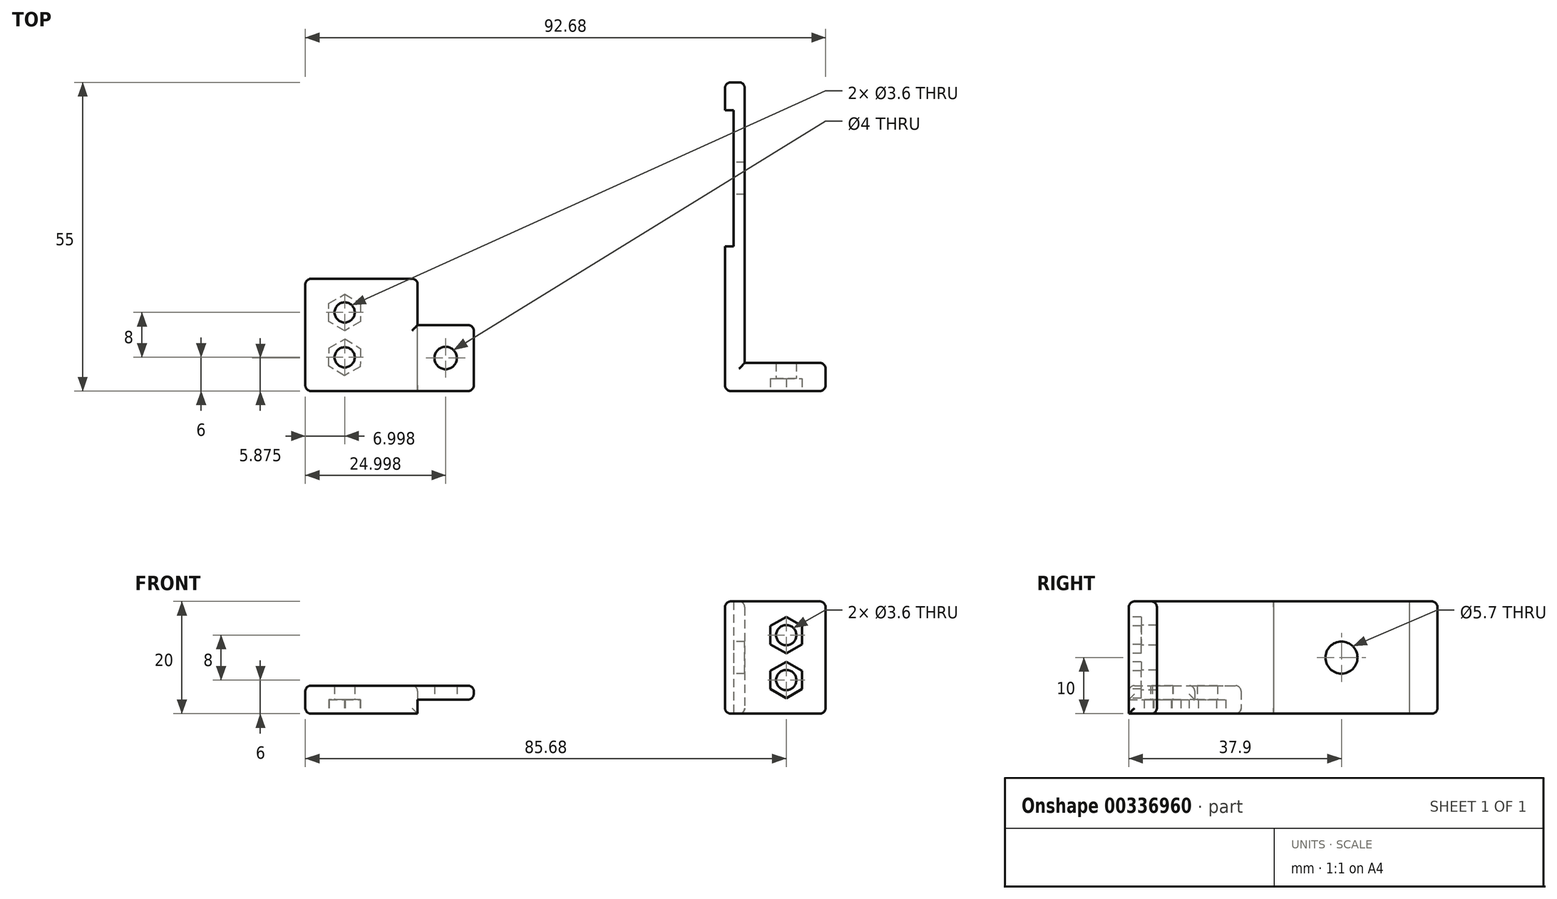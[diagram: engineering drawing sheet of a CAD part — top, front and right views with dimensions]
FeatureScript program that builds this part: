
annotation { "Feature Type Name" : "Feature", "Feature Type Description" : "" }
export const myFeature = defineFeature(function(context is Context, id is Id, definition is map)
    precondition{}
    {
        {
            var Q0;
            Q0=qCreatedBy(makeId("Top.planeOp"),FACE);
            var sketch = newSketch(context, id + "F0", { "sketchPlane" : qUnion([Q0])});
            skLineSegment(sketch, "E0", {"start": v(0, 0) * mm, "end": v(0, 25.8) * mm});
            skLineSegment(sketch, "E1", {"start": v(0, 25.8) * mm, "end": v(1.5, 25.8) * mm});
            skLineSegment(sketch, "E2", {"start": v(1.5, 25.8) * mm, "end": v(1.5, 50) * mm});
            skLineSegment(sketch, "E3", {"start": v(1.5, 50) * mm, "end": v(0, 50) * mm});
            skLineSegment(sketch, "E4", {"start": v(0, 50) * mm, "end": v(0, 55) * mm});
            skLineSegment(sketch, "E5", {"start": v(0, 55) * mm, "end": v(3.5, 55) * mm});
            skLineSegment(sketch, "E6", {"start": v(3.5, 55) * mm, "end": v(3.5, 5) * mm});
            skLineSegment(sketch, "E7", {"start": v(3.5, 5) * mm, "end": v(17.9, 5) * mm});
            skLineSegment(sketch, "E8", {"start": v(17.9, 5) * mm, "end": v(17.9, 0) * mm});
            skLineSegment(sketch, "E9", {"start": v(17.9, 0) * mm, "end": v(0, 0) * mm});
            skLineSegment(sketch, "E10.bottom", {"start": v(-74.78, 0) * mm, "end": v(-54.78, 0) * mm});
            skLineSegment(sketch, "E10.top", {"start": v(-74.78, 20) * mm, "end": v(-54.78, 20) * mm});
            skLineSegment(sketch, "E10.left", {"start": v(-74.78, 0) * mm, "end": v(-74.78, 20) * mm});
            skLineSegment(sketch, "E10.right", {"start": v(-54.78, 0) * mm, "end": v(-54.78, 20) * mm});
            skLineSegment(sketch, "E11.bottom", {"start": v(-54.78, 0) * mm, "end": v(-44.78, 0) * mm});
            skLineSegment(sketch, "E11.top", {"start": v(-54.78, 11.75) * mm, "end": v(-44.78, 11.75) * mm});
            skLineSegment(sketch, "E11.left", {"start": v(-54.78, 0) * mm, "end": v(-54.78, 11.75) * mm});
            skLineSegment(sketch, "E11.right", {"start": v(-44.78, 0) * mm, "end": v(-44.78, 11.75) * mm});
            skLineSegment(sketch, "E12", {"start": v(-67.78, 20) * mm, "end": v(-67.78, 0) * mm, "construction": true});
            skCircle(sketch, "E13", {"center": v(-67.78, 6) * mm, "radius": 1.8 * mm});
            skCircle(sketch, "E14", {"center": v(-67.78, 14) * mm, "radius": 1.8 * mm});
            skCircle(sketch, "E15.cCircle", {"center": v(-67.78, 14) * mm, "radius": 3.25 * mm, "construction": true});
            skLineSegment(sketch, "E15.0", {"start": v(-67.78, 10.75) * mm, "end": v(-70.6, 12.37) * mm});
            skLineSegment(sketch, "E15.1", {"start": v(-70.6, 12.38) * mm, "end": v(-70.6, 15.62) * mm});
            skLineSegment(sketch, "E15.2", {"start": v(-70.6, 15.63) * mm, "end": v(-67.78, 17.25) * mm});
            skLineSegment(sketch, "E15.3", {"start": v(-67.78, 17.25) * mm, "end": v(-64.97, 15.62) * mm});
            skLineSegment(sketch, "E15.4", {"start": v(-64.97, 15.62) * mm, "end": v(-64.97, 12.37) * mm});
            skLineSegment(sketch, "E15.5", {"start": v(-64.97, 12.37) * mm, "end": v(-67.78, 10.75) * mm});
            skCircle(sketch, "E16.cCircle", {"center": v(-67.78, 6) * mm, "radius": 3.25 * mm, "construction": true});
            skLineSegment(sketch, "E16.0", {"start": v(-70.56, 7.68) * mm, "end": v(-67.71, 9.25) * mm});
            skLineSegment(sketch, "E16.1", {"start": v(-67.71, 9.25) * mm, "end": v(-64.93, 7.56) * mm});
            skLineSegment(sketch, "E16.2", {"start": v(-64.93, 7.56) * mm, "end": v(-65, 4.32) * mm});
            skLineSegment(sketch, "E16.3", {"start": v(-65, 4.32) * mm, "end": v(-67.85, 2.75) * mm});
            skLineSegment(sketch, "E16.4", {"start": v(-67.85, 2.75) * mm, "end": v(-70.63, 4.44) * mm});
            skLineSegment(sketch, "E16.5", {"start": v(-70.63, 4.44) * mm, "end": v(-70.56, 7.68) * mm});
            skCircle(sketch, "E17", {"center": v(-49.78, 5.87) * mm, "radius": 2 * mm});
            skPoint(sketch, "E17.centerSnap0", {"position": v(-44.78, 5.87) * mm});
            skPoint(sketch, "E17.centerSnap1", {"position": v(-49.78, 11.75) * mm});
            skSolve(sketch);
        }
        {
            var Q0;
            Q0=makeQuery(id+"F0.imprint","IMPRINT",FACE,{"disambiguationData":[TD([[makeQuery(id+"F0.imprint","IMPRINT",EDGE,{"derivedFrom":sQuery(id+"F0.wireOp",EDGE,"E0")}),-1.0]])]});
            extrude(context, id + "F1", {"entities" : qUnion([Q0]), "depth" : 20 * mm});
        }
        {
            var Q0;
            Q0=makeQuery(id+"F1.opExtrude","SWEPT_FACE",FACE,{"disambiguationData":[OSD([sQuery(id+"F0.wireOp",EDGE,"E9")])]});
            var sketch = newSketch(context, id + "F2", { "sketchPlane" : qUnion([Q0])});
            skLineSegment(sketch, "E18", {"start": v(10.9, 0) * mm, "end": v(10.9, 20) * mm, "construction": true});
            skCircle(sketch, "E19", {"center": v(10.9, 6) * mm, "radius": 1.8 * mm});
            skCircle(sketch, "E20", {"center": v(10.9, 14) * mm, "radius": 1.8 * mm});
            skCircle(sketch, "E21.cCircle", {"center": v(10.9, 14) * mm, "radius": 3.25 * mm, "construction": true});
            skLineSegment(sketch, "E21.0", {"start": v(10.9, 10.75) * mm, "end": v(8.09, 12.37) * mm});
            skLineSegment(sketch, "E21.1", {"start": v(8.09, 12.38) * mm, "end": v(8.09, 15.62) * mm});
            skLineSegment(sketch, "E21.2", {"start": v(8.09, 15.62) * mm, "end": v(10.9, 17.25) * mm});
            skLineSegment(sketch, "E21.3", {"start": v(10.9, 17.25) * mm, "end": v(13.71, 15.62) * mm});
            skLineSegment(sketch, "E21.4", {"start": v(13.71, 15.62) * mm, "end": v(13.71, 12.37) * mm});
            skLineSegment(sketch, "E21.5", {"start": v(13.71, 12.38) * mm, "end": v(10.9, 10.75) * mm});
            skCircle(sketch, "E22.cCircle", {"center": v(10.9, 6) * mm, "radius": 3.25 * mm, "construction": true});
            skLineSegment(sketch, "E22.0", {"start": v(10.9, 9.25) * mm, "end": v(13.71, 7.63) * mm});
            skLineSegment(sketch, "E22.1", {"start": v(13.71, 7.63) * mm, "end": v(13.71, 4.38) * mm});
            skLineSegment(sketch, "E22.2", {"start": v(13.71, 4.38) * mm, "end": v(10.9, 2.75) * mm});
            skLineSegment(sketch, "E22.3", {"start": v(10.9, 2.75) * mm, "end": v(8.09, 4.37) * mm});
            skLineSegment(sketch, "E22.4", {"start": v(8.09, 4.37) * mm, "end": v(8.09, 7.62) * mm});
            skLineSegment(sketch, "E22.5", {"start": v(8.09, 7.62) * mm, "end": v(10.9, 9.25) * mm});
            skSolve(sketch);
        }
        {
            var Q0;
            Q0=makeQuery(id+"F2.imprint","IMPRINT",FACE,{"disambiguationData":[TD([[makeQuery(id+"F2.imprint","IMPRINT",EDGE,{"derivedFrom":sQuery(id+"F2.wireOp",EDGE,"E19")}),1.0]])]});
            var Q1;
            Q1=makeQuery(id+"F2.imprint","IMPRINT",FACE,{"disambiguationData":[TD([[makeQuery(id+"F2.imprint","IMPRINT",EDGE,{"derivedFrom":sQuery(id+"F2.wireOp",EDGE,"E20")}),1.0]])]});
            extrude(context, id + "F3", {"entities" : qUnion([Q0, Q1]), "operationType" : NewBodyOperationType.REMOVE, "oppositeDirection" : true, "depth" : 5 * mm});
        }
        {
            var Q0;
            Q0=makeQuery(id+"F2.imprint","IMPRINT",FACE,{"disambiguationData":[TD([[makeQuery(id+"F2.imprint","IMPRINT",EDGE,{"derivedFrom":sQuery(id+"F2.wireOp",EDGE,"E20")}),-1.0]])]});
            var Q1;
            Q1=makeQuery(id+"F2.imprint","IMPRINT",FACE,{"disambiguationData":[TD([[makeQuery(id+"F2.imprint","IMPRINT",EDGE,{"derivedFrom":sQuery(id+"F2.wireOp",EDGE,"E19")}),-1.0]])]});
            extrude(context, id + "F4", {"entities" : qUnion([Q0, Q1]), "operationType" : NewBodyOperationType.REMOVE, "oppositeDirection" : true, "depth" : 2.2 * mm});
        }
        {
            var Q0;
            Q0=makeQuery(id+"F1.opExtrude","SWEPT_FACE",FACE,{"disambiguationData":[OSD([sQuery(id+"F0.wireOp",EDGE,"E2")])]});
            var sketch = newSketch(context, id + "F5", { "sketchPlane" : qUnion([Q0])});
            skLineSegment(sketch, "E23", {"start": v(-50, 10) * mm, "end": v(-25.8, 10) * mm, "construction": true});
            skCircle(sketch, "E24", {"center": v(-37.9, 10) * mm, "radius": 2.85 * mm});
            skSolve(sketch);
        }
        {
            var Q0;
            Q0=makeQuery(id+"F5.imprint","IMPRINT",FACE,{"disambiguationData":[TD([[makeQuery(id+"F5.imprint","IMPRINT",EDGE,{"derivedFrom":sQuery(id+"F5.wireOp",EDGE,"E24")}),1.0]])]});
            extrude(context, id + "F6", {"entities" : qUnion([Q0]), "operationType" : NewBodyOperationType.REMOVE, "oppositeDirection" : true, "depth" : 25 * mm});
        }
        {
            var Q0;
            Q0=makeQuery(id+"F1.opExtrude","CAP_EDGE",EDGE,{"disambiguationData":[OSD([sQuery(id+"F0.wireOp",EDGE,"E7")])],"isStart":false});
            var Q1;
            Q1=makeQuery(id+"F1.opExtrude","CAP_EDGE",EDGE,{"disambiguationData":[OSD([sQuery(id+"F0.wireOp",EDGE,"E6")])],"isStart":false});
            var Q2;
            Q2=makeQuery(id+"F1.opExtrude","SWEPT_EDGE",EDGE,{"disambiguationData":[OSD([sQuery(id+"F0.wireOp",EDGE,"E5"),sQuery(id+"F0.wireOp",EDGE,"E6")])]});
            var Q3;
            Q3=makeQuery(id+"F1.opExtrude","CAP_EDGE",EDGE,{"disambiguationData":[OSD([sQuery(id+"F0.wireOp",EDGE,"E5")])],"isStart":false});
            var Q4;
            Q4=makeQuery(id+"F1.opExtrude","SWEPT_EDGE",EDGE,{"disambiguationData":[OSD([sQuery(id+"F0.wireOp",EDGE,"E4"),sQuery(id+"F0.wireOp",EDGE,"E5")])]});
            var Q5;
            Q5=makeQuery(id+"F1.opExtrude","CAP_EDGE",EDGE,{"disambiguationData":[OSD([sQuery(id+"F0.wireOp",EDGE,"E5")])],"isStart":true});
            var Q6;
            Q6=makeQuery(id+"F1.opExtrude","CAP_EDGE",EDGE,{"disambiguationData":[OSD([sQuery(id+"F0.wireOp",EDGE,"E6")])],"isStart":true});
            var Q7;
            Q7=makeQuery(id+"F1.opExtrude","CAP_EDGE",EDGE,{"disambiguationData":[OSD([sQuery(id+"F0.wireOp",EDGE,"E7")])],"isStart":true});
            var Q8;
            Q8=makeQuery(id+"F1.opExtrude","SWEPT_EDGE",EDGE,{"disambiguationData":[OSD([sQuery(id+"F0.wireOp",EDGE,"E7"),sQuery(id+"F0.wireOp",EDGE,"E8")])]});
            var Q9;
            Q9=makeQuery(id+"F1.opExtrude","CAP_EDGE",EDGE,{"disambiguationData":[OSD([sQuery(id+"F0.wireOp",EDGE,"E8")])],"isStart":true});
            var Q10;
            Q10=makeQuery(id+"F1.opExtrude","CAP_EDGE",EDGE,{"disambiguationData":[OSD([sQuery(id+"F0.wireOp",EDGE,"E8")])],"isStart":false});
            var Q11;
            Q11=makeQuery(id+"F1.opExtrude","SWEPT_EDGE",EDGE,{"disambiguationData":[OSD([sQuery(id+"F0.wireOp",EDGE,"E8"),sQuery(id+"F0.wireOp",EDGE,"E9")])]});
            var Q12;
            Q12=makeQuery(id+"F1.opExtrude","CAP_EDGE",EDGE,{"disambiguationData":[OSD([sQuery(id+"F0.wireOp",EDGE,"E0")])],"isStart":false});
            var Q13;
            Q13=makeQuery(id+"F1.opExtrude","CAP_EDGE",EDGE,{"disambiguationData":[OSD([sQuery(id+"F0.wireOp",EDGE,"E9")])],"isStart":false});
            var Q14;
            Q14=makeQuery(id+"F1.opExtrude","CAP_EDGE",EDGE,{"disambiguationData":[OSD([sQuery(id+"F0.wireOp",EDGE,"E4")])],"isStart":false});
            var Q15;
            Q15=makeQuery(id+"F1.opExtrude","CAP_EDGE",EDGE,{"disambiguationData":[OSD([sQuery(id+"F0.wireOp",EDGE,"E0")])],"isStart":true});
            var Q16;
            Q16=makeQuery(id+"F1.opExtrude","SWEPT_EDGE",EDGE,{"disambiguationData":[OSD([sQuery(id+"F0.wireOp",EDGE,"E0"),sQuery(id+"F0.wireOp",EDGE,"E9")])]});
            var Q17;
            Q17=makeQuery(id+"F1.opExtrude","CAP_EDGE",EDGE,{"disambiguationData":[OSD([sQuery(id+"F0.wireOp",EDGE,"E4")])],"isStart":true});
            fillet(context, id + "F7", {"entities" : qUnion([Q0, Q1, Q2, Q3, Q4, Q5, Q6, Q7, Q8, Q9, Q10, Q11, Q12, Q13, Q14, Q15, Q16, Q17]), "radius" : 1 * mm, "tangentPropagation" : true, "allowEdgeOverflow" : false});
        }
        {
            var Q0;
            Q0=makeQuery(id+"F0.imprint","IMPRINT",FACE,{"disambiguationData":[TD([[makeQuery(id+"F0.imprint","IMPRINT",EDGE,{"derivedFrom":sQuery(id+"F0.wireOp",EDGE,"E10.bottom")}),1.0]])]});
            extrude(context, id + "F8", {"entities" : qUnion([Q0]), "depth" : 5 * mm});
        }
        {
            var Q0;
            Q0=makeQuery(id+"F0.imprint","IMPRINT",FACE,{"disambiguationData":[TD([[makeQuery(id+"F0.imprint","IMPRINT",EDGE,{"derivedFrom":sQuery(id+"F0.wireOp",EDGE,"E13")}),-1.0]])]});
            var Q1;
            Q1=makeQuery(id+"F0.imprint","IMPRINT",FACE,{"disambiguationData":[TD([[makeQuery(id+"F0.imprint","IMPRINT",EDGE,{"derivedFrom":sQuery(id+"F0.wireOp",EDGE,"E14")}),-1.0]])]});
            extrude(context, id + "F9", {"entities" : qUnion([Q0, Q1]), "operationType" : NewBodyOperationType.ADD, "depth" : 5 * mm, "hasSecondDirection" : true, "secondDirectionOppositeDirection" : false, "secondDirectionDepth" : 2.5 * mm});
        }
        {
            var Q0;
            Q0=makeQuery(id+"F0.imprint","IMPRINT",FACE,{"disambiguationData":[TD([[makeQuery(id+"F0.imprint","IMPRINT",EDGE,{"derivedFrom":sQuery(id+"F0.wireOp",EDGE,"E11.bottom")}),1.0]])]});
            extrude(context, id + "F10", {"entities" : qUnion([Q0]), "operationType" : NewBodyOperationType.ADD, "depth" : 5 * mm, "hasSecondDirection" : true, "secondDirectionOppositeDirection" : false, "secondDirectionDepth" : 2.5 * mm});
        }
        {
            var Q0;
            Q0=makeQuery(id+"F10.boolean.opBoolean","MERGE",EDGE,{"derivedFrom":[makeQuery(id+"F8.opExtrude","CAP_EDGE",EDGE,{"disambiguationData":[OSD([sQuery(id+"F0.wireOp",EDGE,"E10.bottom")])],"isStart":false}),makeQuery(id+"F10.opExtrude","CAP_EDGE",EDGE,{"disambiguationData":[OSD([sQuery(id+"F0.wireOp",EDGE,"E11.bottom")])],"isStart":false})]});
            var Q1;
            Q1=makeQuery(id+"F8.opExtrude","CAP_EDGE",EDGE,{"disambiguationData":[OSD([sQuery(id+"F0.wireOp",EDGE,"E10.bottom")])],"isStart":true});
            var Q2;
            Q2=makeQuery(id+"F10.opExtrude","SWEPT_EDGE",EDGE,{"disambiguationData":[OSD([sQuery(id+"F0.wireOp",EDGE,"E11.bottom"),sQuery(id+"F0.wireOp",EDGE,"E11.right")])]});
            var Q3;
            Q3=makeQuery(id+"F10.opExtrude","CAP_EDGE",EDGE,{"disambiguationData":[OSD([sQuery(id+"F0.wireOp",EDGE,"E11.right")])],"isStart":false});
            var Q4;
            Q4=makeQuery(id+"F10.opExtrude","CAP_EDGE",EDGE,{"disambiguationData":[OSD([sQuery(id+"F0.wireOp",EDGE,"E11.top")])],"isStart":false});
            var Q5;
            Q5=makeQuery(id+"F8.opExtrude","CAP_EDGE",EDGE,{"disambiguationData":[OSD([sQuery(id+"F0.wireOp",EDGE,"E10.right"),sQuery(id+"F0.wireOp",EDGE,"E11.left")])],"isStart":false});
            var Q6;
            Q6=makeQuery(id+"F8.opExtrude","CAP_EDGE",EDGE,{"disambiguationData":[OSD([sQuery(id+"F0.wireOp",EDGE,"E10.left")])],"isStart":false});
            var Q7;
            Q7=makeQuery(id+"F8.opExtrude","CAP_EDGE",EDGE,{"disambiguationData":[OSD([sQuery(id+"F0.wireOp",EDGE,"E10.top")])],"isStart":false});
            var Q8;
            Q8=makeQuery(id+"F8.opExtrude","SWEPT_EDGE",EDGE,{"disambiguationData":[OSD([sQuery(id+"F0.wireOp",EDGE,"E10.bottom"),sQuery(id+"F0.wireOp",EDGE,"E10.left")])]});
            var Q9;
            Q9=makeQuery(id+"F8.opExtrude","CAP_EDGE",EDGE,{"disambiguationData":[OSD([sQuery(id+"F0.wireOp",EDGE,"E10.left")])],"isStart":true});
            var Q10;
            Q10=makeQuery(id+"F10.opExtrude","CAP_EDGE",EDGE,{"disambiguationData":[OSD([sQuery(id+"F0.wireOp",EDGE,"E11.right")])],"isStart":true});
            var Q11;
            Q11=makeQuery(id+"F10.opExtrude","SWEPT_EDGE",EDGE,{"disambiguationData":[OSD([sQuery(id+"F0.wireOp",EDGE,"E11.top"),sQuery(id+"F0.wireOp",EDGE,"E11.right")])]});
            var Q12;
            Q12=makeQuery(id+"F10.opExtrude","SWEPT_EDGE",EDGE,{"disambiguationData":[OSD([sQuery(id+"F0.wireOp",EDGE,"E10.right"),sQuery(id+"F0.wireOp",EDGE,"E11.top"),sQuery(id+"F0.wireOp",EDGE,"E11.left")])]});
            var Q13;
            Q13=makeQuery(id+"F8.opExtrude","CAP_EDGE",EDGE,{"disambiguationData":[OSD([sQuery(id+"F0.wireOp",EDGE,"E10.top")])],"isStart":true});
            var Q14;
            Q14=makeQuery(id+"F8.opExtrude","SWEPT_EDGE",EDGE,{"disambiguationData":[OSD([sQuery(id+"F0.wireOp",EDGE,"E10.top"),sQuery(id+"F0.wireOp",EDGE,"E10.right")])]});
            var Q15;
            Q15=makeQuery(id+"F8.opExtrude","SWEPT_EDGE",EDGE,{"disambiguationData":[OSD([sQuery(id+"F0.wireOp",EDGE,"E10.top"),sQuery(id+"F0.wireOp",EDGE,"E10.left")])]});
            fillet(context, id + "F11", {"entities" : qUnion([Q0, Q1, Q2, Q3, Q4, Q5, Q6, Q7, Q8, Q9, Q10, Q11, Q12, Q13, Q14, Q15]), "radius" : 1 * mm, "tangentPropagation" : true, "allowEdgeOverflow" : false});
        }
    });
